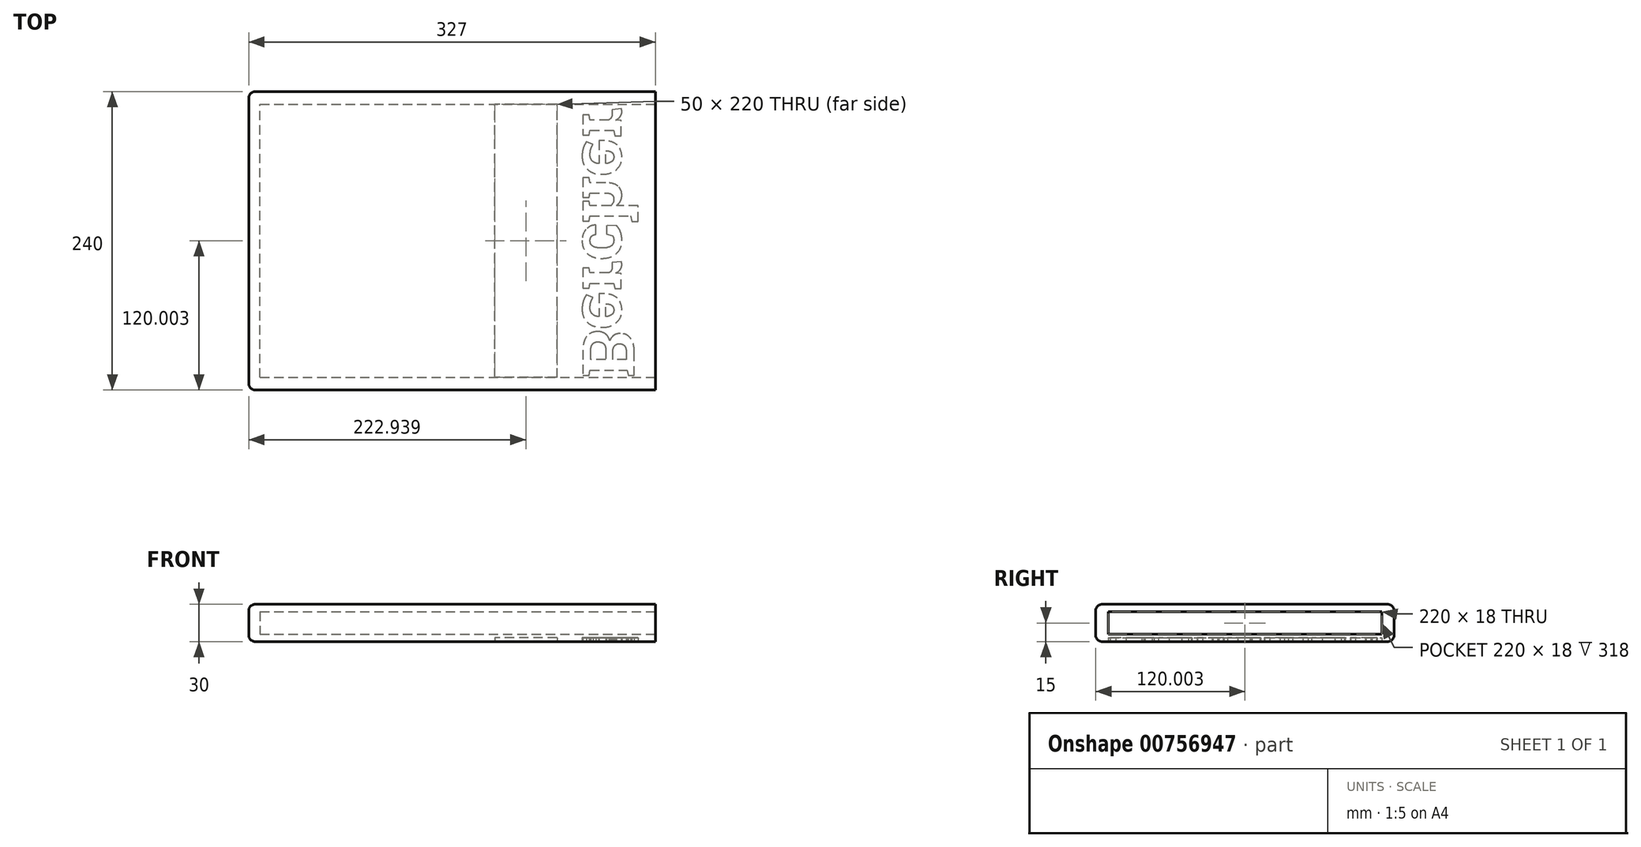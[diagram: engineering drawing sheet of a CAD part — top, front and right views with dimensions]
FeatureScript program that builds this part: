
annotation { "Feature Type Name" : "Feature", "Feature Type Description" : "" }
export const myFeature = defineFeature(function(context is Context, id is Id, definition is map)
    precondition{}
    {
        {
            var Q0;
            Q0=qCreatedBy(makeId("Top.planeOp"),FACE);
            var sketch = newSketch(context, id + "F0", { "sketchPlane" : qUnion([Q0])});
            skLineSegment(sketch, "E0.bottom", {"start": v(-86.6, 156.7) * mm, "end": v(240.4, 156.7) * mm});
            skLineSegment(sketch, "E0.top", {"start": v(-86.6, -83.3) * mm, "end": v(240.4, -83.3) * mm});
            skLineSegment(sketch, "E0.left", {"start": v(-86.6, 156.7) * mm, "end": v(-86.6, -83.3) * mm});
            skLineSegment(sketch, "E0.right", {"start": v(240.4, 156.7) * mm, "end": v(240.4, -83.3) * mm});
            skSolve(sketch);
        }
        {
            var Q0;
            Q0=qSketchRegion(id+"F0",true);
            extrude(context, id + "F1", {"entities" : qUnion([Q0]), "depth" : 30 * mm, "offsetDistance" : 25 * mm});
        }
        {
            var Q0;
            Q0=makeQuery(id+"F1.opExtrude","SWEPT_FACE",FACE,{"disambiguationData":[OSD([sQuery(id+"F0.wireOp",EDGE,"E0.right")])]});
            var sketch = newSketch(context, id + "F2", { "sketchPlane" : qUnion([Q0])});
            skLineSegment(sketch, "E1.bottom", {"start": v(-73.3, 24) * mm, "end": v(146.7, 24) * mm});
            skLineSegment(sketch, "E1.top", {"start": v(-73.3, 6) * mm, "end": v(146.7, 6) * mm});
            skLineSegment(sketch, "E1.left", {"start": v(-73.3, 24) * mm, "end": v(-73.3, 6) * mm});
            skLineSegment(sketch, "E1.right", {"start": v(146.7, 24) * mm, "end": v(146.7, 6) * mm});
            skSolve(sketch);
        }
        {
            var Q0;
            Q0=qSketchRegion(id+"F2",true);
            extrude(context, id + "F3", {"entities" : qUnion([Q0]), "operationType" : NewBodyOperationType.REMOVE, "oppositeDirection" : true, "depth" : 318 * mm, "offsetDistance" : 25 * mm});
        }
        {
            var Q0;
            Q0=makeQuery(id+"F1.opExtrude","CAP_EDGE",EDGE,{"disambiguationData":[OSD([sQuery(id+"F0.wireOp",EDGE,"E0.left")])],"isStart":false});
            var Q1;
            Q1=makeQuery(id+"F1.opExtrude","CAP_EDGE",EDGE,{"disambiguationData":[OSD([sQuery(id+"F0.wireOp",EDGE,"E0.top")])],"isStart":false});
            var Q2;
            Q2=makeQuery(id+"F1.opExtrude","CAP_EDGE",EDGE,{"disambiguationData":[OSD([sQuery(id+"F0.wireOp",EDGE,"E0.bottom")])],"isStart":false});
            var Q3;
            Q3=makeQuery(id+"F1.opExtrude","CAP_EDGE",EDGE,{"disambiguationData":[OSD([sQuery(id+"F0.wireOp",EDGE,"E0.left")])],"isStart":true});
            var Q4;
            Q4=makeQuery(id+"F1.opExtrude","CAP_EDGE",EDGE,{"disambiguationData":[OSD([sQuery(id+"F0.wireOp",EDGE,"E0.bottom")])],"isStart":true});
            var Q5;
            Q5=makeQuery(id+"F1.opExtrude","CAP_EDGE",EDGE,{"disambiguationData":[OSD([sQuery(id+"F0.wireOp",EDGE,"E0.top")])],"isStart":true});
            var Q6;
            Q6=makeQuery(id+"F1.opExtrude","SWEPT_EDGE",EDGE,{"disambiguationData":[OSD([sQuery(id+"F0.wireOp",EDGE,"E0.bottom"),sQuery(id+"F0.wireOp",EDGE,"E0.left")])]});
            var Q7;
            Q7=makeQuery(id+"F1.opExtrude","SWEPT_EDGE",EDGE,{"disambiguationData":[OSD([sQuery(id+"F0.wireOp",EDGE,"E0.top"),sQuery(id+"F0.wireOp",EDGE,"E0.left")])]});
            fillet(context, id + "F4", {"entities" : qUnion([Q0, Q1, Q2, Q3, Q4, Q5, Q6, Q7]), "radius" : 5 * mm, "tangentPropagation" : true, "allowEdgeOverflow" : false});
        }
        {
            var Q0;
            Q0=makeQuery(id+"F1.opExtrude","CAP_FACE",FACE,{"disambiguationData":[OSD([sQuery(id+"F0.wireOp",EDGE,"E0.bottom"),sQuery(id+"F0.wireOp",EDGE,"E0.top"),sQuery(id+"F0.wireOp",EDGE,"E0.left"),sQuery(id+"F0.wireOp",EDGE,"E0.right")])],"isStart":true});
            var sketch = newSketch(context, id + "F5", { "sketchPlane" : qUnion([Q0])});
            skText(sketch, "E2", { "text": "Bercher", "fontName": "RobotoSlab-Bold.ttf"});
            const initialGuessF5  = {"E2": [0.18215, 0.0733, 0, -1, 0.0419]};
            skSetInitialGuess(sketch, initialGuessF5);
            skSolve(sketch);
        }
        {
            var Q0;
            Q0=qSketchRegion(id+"F5",true);
            extrude(context, id + "F6", {"entities" : qUnion([Q0]), "operationType" : NewBodyOperationType.REMOVE, "oppositeDirection" : true, "depth" : 3 * mm, "offsetDistance" : 25 * mm});
        }
        {
            var Q0;
            {var subQ0=sQuery(id+"F0.wireOp",EDGE,"E0.bottom");var subQ1=sQuery(id+"F0.wireOp",EDGE,"E0.left");var subQ2=sQuery(id+"F0.wireOp",EDGE,"E0.top");var subQ3=sQuery(id+"F0.wireOp",EDGE,"E0.right");Q0=makeQuery(id+"F6.boolean.opBoolean","SPLIT",FACE,{"disambiguationData":[TD([makeQuery(id+"F1.opExtrude","SWEPT_FACE",FACE,{"disambiguationData":[OSD([subQ3])]})])],"derivedFrom":makeQuery(id+"F1.opExtrude","CAP_FACE",FACE,{"disambiguationData":[OSD([subQ0,subQ2,subQ1,subQ3])],"isStart":true})});}
            var sketch = newSketch(context, id + "F7", { "sketchPlane" : qUnion([Q0])});
            skLineSegment(sketch, "E3.bottom", {"start": v(161.34, 73.3) * mm, "end": v(111.34, 73.3) * mm});
            skLineSegment(sketch, "E3.top", {"start": v(161.34, -146.7) * mm, "end": v(111.34, -146.7) * mm});
            skLineSegment(sketch, "E3.left", {"start": v(161.34, 73.3) * mm, "end": v(161.34, -146.7) * mm});
            skLineSegment(sketch, "E3.right", {"start": v(111.34, 73.3) * mm, "end": v(111.34, -146.7) * mm});
            skSolve(sketch);
        }
        {
            var Q0;
            Q0=makeQuery(id+"F7.imprint","IMPRINT",FACE,{"disambiguationData":[TD([[makeQuery(id+"F7.imprint","IMPRINT",EDGE,{"derivedFrom":sQuery(id+"F7.wireOp",EDGE,"E3.bottom")}),1.0]])]});
            extrude(context, id + "F8", {"entities" : qUnion([Q0]), "operationType" : NewBodyOperationType.REMOVE, "oppositeDirection" : true, "depth" : 3 * mm, "offsetDistance" : 25 * mm});
        }
    });
